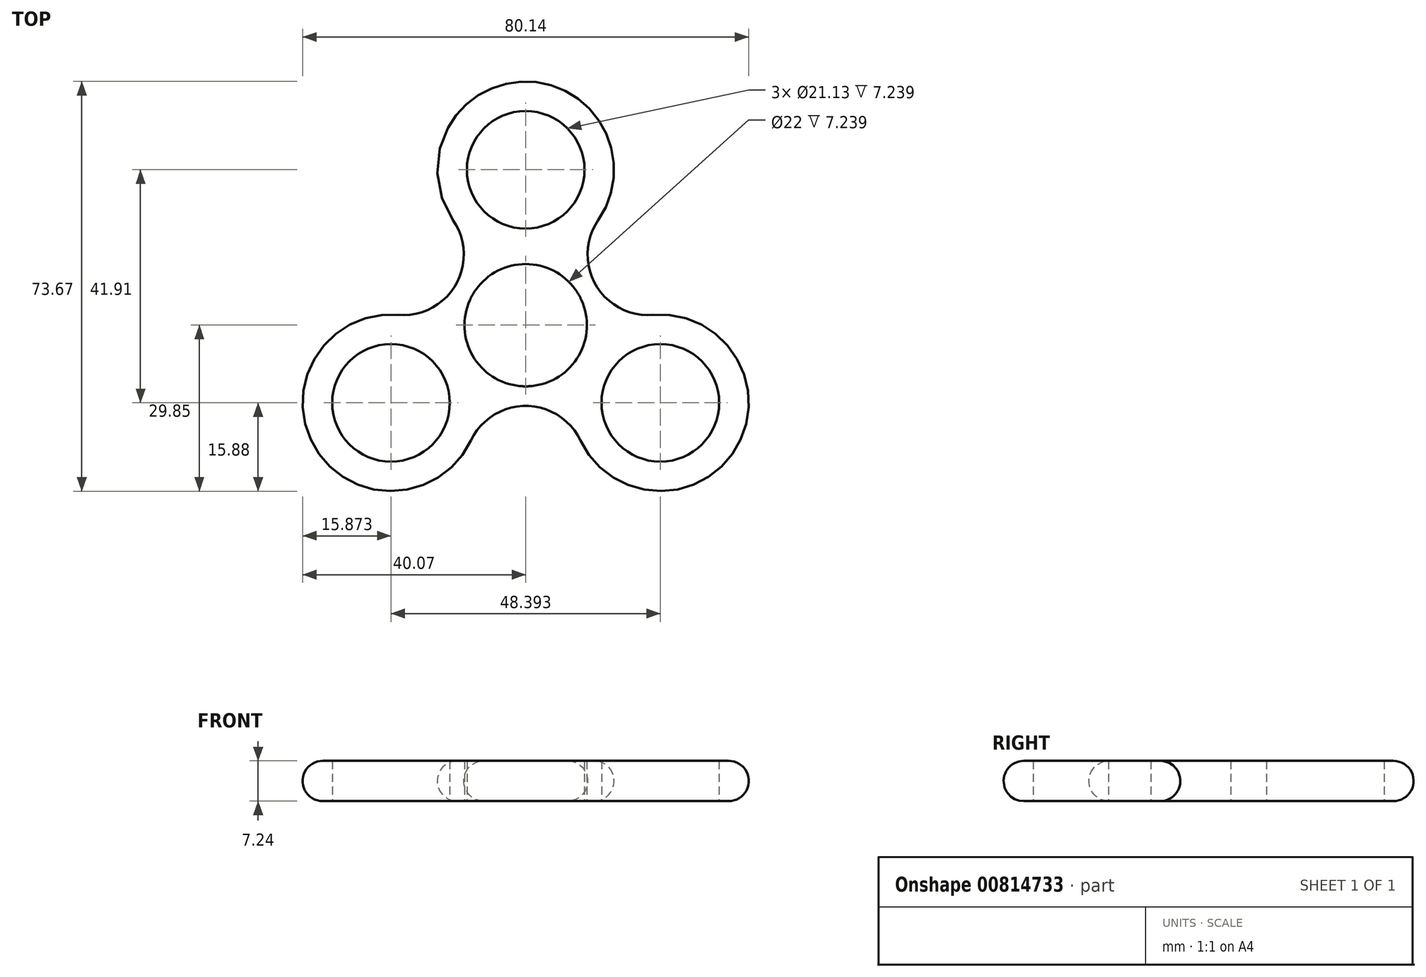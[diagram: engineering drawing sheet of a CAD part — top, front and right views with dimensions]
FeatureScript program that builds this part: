
annotation { "Feature Type Name" : "Feature", "Feature Type Description" : "" }
export const myFeature = defineFeature(function(context is Context, id is Id, definition is map)
    precondition{}
    {
        {
            var Q0;
            Q0=qCreatedBy(makeId("Top.planeOp"),FACE);
            var sketch = newSketch(context, id + "F0", { "sketchPlane" : qUnion([Q0])});
            skCircle(sketch, "E0", {"center": v(0, 0) * mm, "radius": 11 * mm});
            skCircle(sketch, "E1", {"center": v(0, 27.94) * mm, "radius": 10.57 * mm});
            skCircle(sketch, "E2", {"center": v(0, 0) * mm, "radius": 43.82 * mm, "construction": true});
            skLineSegment(sketch, "E3.anchor1", {"start": v(0, 0) * mm, "end": v(0, 27.94) * mm, "construction": true});
            skCircle(sketch, "E4", {"center": v(0, 27.94) * mm, "radius": 15.88 * mm});
            skCircle(sketch, "E5.1.0", {"center": v(-24.2, -13.97) * mm, "radius": 10.57 * mm});
            skCircle(sketch, "E5.1.1", {"center": v(-24.2, -13.97) * mm, "radius": 15.88 * mm});
            skCircle(sketch, "E5.2.0", {"center": v(24.2, -13.97) * mm, "radius": 10.57 * mm});
            skCircle(sketch, "E5.2.1", {"center": v(24.2, -13.97) * mm, "radius": 15.88 * mm});
            skLineSegment(sketch, "E6", {"start": v(0, 0) * mm, "end": v(0, -43.82) * mm, "construction": true});
            skArc(sketch, "E7", {"start": v(9.84, -20.75) * mm, "mid": v(0, -14.51) * mm, "end": v(-9.84, -20.75) * mm});
            skArc(sketch, "E8.1.0", {"start": v(-22.9, 1.85) * mm, "mid": v(-12.57, 7.26) * mm, "end": v(-13.05, 18.9) * mm});
            skArc(sketch, "E8.2.0", {"start": v(13.05, 18.9) * mm, "mid": v(12.57, 7.26) * mm, "end": v(22.9, 1.85) * mm});
            skLineSegment(sketch, "E8.anchor1", {"start": v(0, 0) * mm, "end": v(-9.84, -20.75) * mm, "construction": true});
            skLineSegment(sketch, "E8.anchor2", {"start": v(0, 0) * mm, "end": v(22.9, 1.85) * mm, "construction": true});
            skSolve(sketch);
        }
        {
            var Q0;
            Q0=makeQuery(id+"F0.imprint","IMPRINT",FACE,{"disambiguationData":[TD([[makeQuery(id+"F0.imprint","IMPRINT",EDGE,{"derivedFrom":sQuery(id+"F0.wireOp",EDGE,"E1")}),-1.0]])]});
            var Q1;
            Q1=makeQuery(id+"F0.imprint","IMPRINT",FACE,{"disambiguationData":[TD([[makeQuery(id+"F0.imprint","IMPRINT",EDGE,{"derivedFrom":sQuery(id+"F0.wireOp",EDGE,"E0")}),-1.0]])]});
            var Q2;
            Q2=makeQuery(id+"F0.imprint","IMPRINT",FACE,{"disambiguationData":[TD([[makeQuery(id+"F0.imprint","IMPRINT",EDGE,{"derivedFrom":sQuery(id+"F0.wireOp",EDGE,"E5.2.0")}),-1.0]])]});
            var Q3;
            Q3=makeQuery(id+"F0.imprint","IMPRINT",FACE,{"disambiguationData":[TD([[makeQuery(id+"F0.imprint","IMPRINT",EDGE,{"derivedFrom":sQuery(id+"F0.wireOp",EDGE,"E5.1.0")}),-1.0]])]});
            extrude(context, id + "F1", {"entities" : qUnion([Q0, Q1, Q2, Q3]), "depth" : 7.24 * mm, "offsetDistance" : 25.4 * mm});
        }
        {
            var Q0;
            Q0=makeQuery(id+"F1.opExtrude","CAP_EDGE",EDGE,{"disambiguationData":[OSD([sQuery(id+"F0.wireOp",EDGE,"E5.1.1")])],"isStart":false});
            var Q1;
            Q1=makeQuery(id+"F1.opExtrude","CAP_EDGE",EDGE,{"disambiguationData":[OSD([sQuery(id+"F0.wireOp",EDGE,"E5.1.1")])],"isStart":true});
            fillet(context, id + "F2", {"entities" : qUnion([Q0, Q1]), "radius" : 3.62 * mm, "tangentPropagation" : true, "allowEdgeOverflow" : false});
        }
    });
